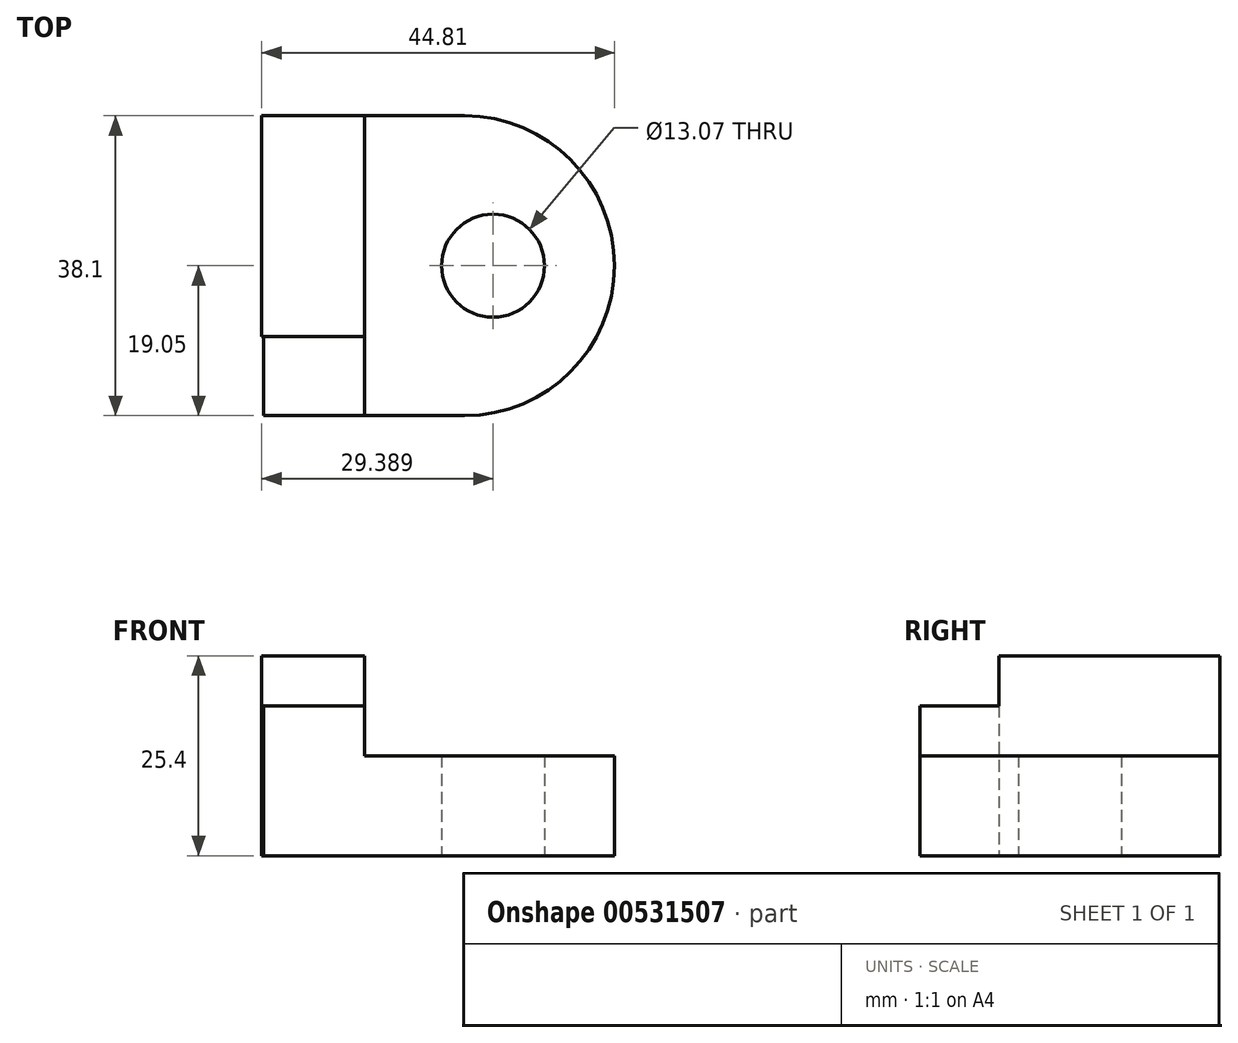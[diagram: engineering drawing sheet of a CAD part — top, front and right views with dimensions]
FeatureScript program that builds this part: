
annotation { "Feature Type Name" : "Feature", "Feature Type Description" : "" }
export const myFeature = defineFeature(function(context is Context, id is Id, definition is map)
    precondition{}
    {
        {
            var Q0;
            Q0=qCreatedBy(makeId("Top.planeOp"),FACE);
            var sketch = newSketch(context, id + "F0", { "sketchPlane" : qUnion([Q0])});
            skLineSegment(sketch, "E0.bottom", {"start": v(12.7, 19.05) * mm, "end": v(-12.7, 19.05) * mm});
            skLineSegment(sketch, "E0.top", {"start": v(12.7, -19.05) * mm, "end": v(-12.7, -19.05) * mm});
            skLineSegment(sketch, "E0.left", {"start": v(12.7, 19.05) * mm, "end": v(12.7, -19.05) * mm});
            skLineSegment(sketch, "E0.right", {"start": v(-12.7, 19.05) * mm, "end": v(-12.7, -19.05) * mm});
            skPoint(sketch, "E0.middle", {"position": v(0, 0) * mm});
            skArc(sketch, "E1", {"start": v(12.7, 19.05) * mm, "mid": v(31.75, 0) * mm, "end": v(12.7, -19.05) * mm});
            skSolve(sketch);
        }
        {
            var Q0;
            Q0=makeQuery(id+"F0.imprint","IMPRINT",FACE,{"disambiguationData":[TD([[makeQuery(id+"F0.imprint","IMPRINT",EDGE,{"derivedFrom":sQuery(id+"F0.wireOp",EDGE,"E0.bottom")}),1.0]])]});
            var Q1;
            Q1=makeQuery(id+"F0.imprint","IMPRINT",FACE,{"disambiguationData":[TD([[makeQuery(id+"F0.imprint","IMPRINT",EDGE,{"derivedFrom":sQuery(id+"F0.wireOp",EDGE,"E0.left")}),1.0]])]});
            extrude(context, id + "F1", {"entities" : qUnion([Q0, Q1]), "depth" : 12.7 * mm, "offsetDistance" : 25.4 * mm});
        }
        {
            var Q0;
            Q0=qCreatedBy(makeId("Top.planeOp"),FACE);
            var sketch = newSketch(context, id + "F2", { "sketchPlane" : qUnion([Q0])});
            skCircle(sketch, "E2", {"center": v(16.33, 0) * mm, "radius": 6.54 * mm});
            skSolve(sketch);
        }
        {
            var Q0;
            Q0=makeQuery(id+"F2.imprint","IMPRINT",FACE,{"disambiguationData":[TD([[makeQuery(id+"F2.imprint","IMPRINT",EDGE,{"derivedFrom":sQuery(id+"F2.wireOp",EDGE,"E2")}),1.0]])]});
            extrude(context, id + "F3", {"entities" : qUnion([Q0]), "operationType" : NewBodyOperationType.REMOVE, "endBound" : BoundingType.THROUGH_ALL, "depth" : 25.4 * mm, "offsetDistance" : 25.4 * mm});
        }
        {
            var Q0;
            Q0=qCreatedBy(makeId("Top.planeOp"),FACE);
            var sketch = newSketch(context, id + "F4", { "sketchPlane" : qUnion([Q0])});
            skLineSegment(sketch, "E3.bottom", {"start": v(0, -8.98) * mm, "end": v(-12.8, -8.98) * mm});
            skLineSegment(sketch, "E3.top", {"start": v(0, 18.78) * mm, "end": v(-12.8, 18.78) * mm});
            skLineSegment(sketch, "E3.left", {"start": v(0, -8.98) * mm, "end": v(0, 18.78) * mm});
            skLineSegment(sketch, "E3.right", {"start": v(-12.8, -8.98) * mm, "end": v(-12.8, 18.78) * mm});
            skLineSegment(sketch, "E4.top", {"start": v(0, -19.05) * mm, "end": v(-12.8, -19.05) * mm});
            skLineSegment(sketch, "E4.left", {"start": v(0, -8.98) * mm, "end": v(0, -19.05) * mm});
            skLineSegment(sketch, "E4.right", {"start": v(-12.8, -8.98) * mm, "end": v(-12.8, -19.05) * mm});
            skSolve(sketch);
        }
        {
            var Q0;
            Q0=makeQuery(id+"F4.imprint","IMPRINT",FACE,{"disambiguationData":[TD([[makeQuery(id+"F4.imprint","IMPRINT",EDGE,{"derivedFrom":sQuery(id+"F4.wireOp",EDGE,"E3.bottom")}),1.0]])]});
            extrude(context, id + "F5", {"entities" : qUnion([Q0]), "operationType" : NewBodyOperationType.ADD, "depth" : 19.05 * mm, "offsetDistance" : 25.4 * mm});
        }
        {
            var Q0;
            Q0=qCreatedBy(makeId("Top.planeOp"),FACE);
            var sketch = newSketch(context, id + "F6", { "sketchPlane" : qUnion([Q0])});
            skLineSegment(sketch, "E5.bottom", {"start": v(-13.06, 19.05) * mm, "end": v(0, 19.05) * mm});
            skLineSegment(sketch, "E5.top", {"start": v(-13.06, -8.98) * mm, "end": v(0, -8.98) * mm});
            skLineSegment(sketch, "E5.left", {"start": v(-13.06, 19.05) * mm, "end": v(-13.06, -8.98) * mm});
            skLineSegment(sketch, "E5.right", {"start": v(0, 19.05) * mm, "end": v(0, -8.98) * mm});
            skSolve(sketch);
        }
        {
            var Q0;
            Q0=makeQuery(id+"F6.imprint","IMPRINT",FACE,{"disambiguationData":[TD([[makeQuery(id+"F6.imprint","IMPRINT",EDGE,{"derivedFrom":sQuery(id+"F6.wireOp",EDGE,"E5.bottom")}),-1.0]])]});
            extrude(context, id + "F7", {"entities" : qUnion([Q0]), "operationType" : NewBodyOperationType.ADD, "depth" : 25.4 * mm, "offsetDistance" : 25.4 * mm});
        }
    });
